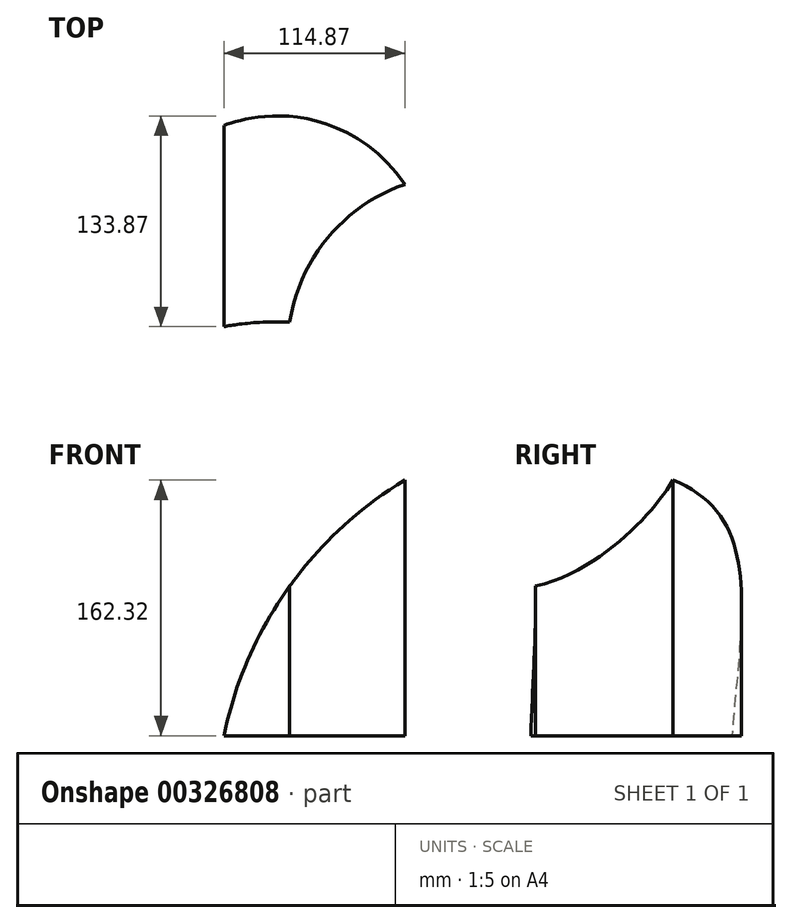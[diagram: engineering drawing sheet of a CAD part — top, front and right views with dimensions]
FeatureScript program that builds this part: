
annotation { "Feature Type Name" : "Feature", "Feature Type Description" : "" }
export const myFeature = defineFeature(function(context is Context, id is Id, definition is map)
    precondition{}
    {
        {
            var Q0;
            Q0=qCreatedBy(makeId("Top.planeOp"),FACE);
            var sketch = newSketch(context, id + "F0", { "sketchPlane" : qUnion([Q0])});
            skCircle(sketch, "E0", {"center": v(0, 280.6) * mm, "radius": 97.28 * mm});
            skCircle(sketch, "E1", {"center": v(117.11, 230) * mm, "radius": 110.4 * mm});
            skCircle(sketch, "E2", {"center": v(0, 58.68) * mm, "radius": 188.4 * mm});
            skSolve(sketch);
        }
        {
            var Q0;
            {var subQ0=sQuery(id+"F0.wireOp",EDGE,"E2");var subQ1=sQuery(id+"F0.wireOp",EDGE,"E0");var subQ2=makeQuery(id+"F0.imprint","INTERSECT",VERTEX,{"disambiguationData":[OD(0.0)],"derivedFrom":[subQ1,subQ0]});Q0=makeQuery(id+"F0.imprint","IMPRINT",FACE,{"disambiguationData":[TD([[makeQuery(id+"F0.imprint","IMPRINT",EDGE,{"disambiguationData":[TD([[subQ2,1.0]])],"derivedFrom":subQ1}),1.0]])]});}
            extrude(context, id + "F1", {"entities" : qUnion([Q0]), "depth" : 168.36 * mm});
        }
        {
            var Q0;
            Q0=qCreatedBy(makeId("Front.planeOp"),FACE);
            var sketch = newSketch(context, id + "F2", { "sketchPlane" : qUnion([Q0])});
            skCircle(sketch, "E3", {"center": v(209.61, -50.43) * mm, "radius": 248.57 * mm});
            skSolve(sketch);
        }
        {
            var Q0;
            Q0 = qSketchRegion(id + "F2", true);
            extrude(context, id + "F3", {"entities" : qUnion([Q0]), "oppositeDirection" : true, "depth" : 465.38 * mm});
        }
        {
            var Q0;
            Q0=makeQuery(id+"F1.opExtrude","SWEPT_BODY",BODY,{"disambiguationData":[OSD([sQuery(id+"F0.wireOp",EDGE,"E0"),sQuery(id+"F0.wireOp",EDGE,"E1"),sQuery(id+"F0.wireOp",EDGE,"E2")])]});
            var Q1;
            Q1=makeQuery(id+"F3.opExtrude","SWEPT_BODY",BODY,{"disambiguationData":[OSD([sQuery(id+"F2.wireOp",EDGE,"E3")])]});
            booleanBodies(context, id + "F4", {"operationType" : BooleanOperationType.INTERSECTION, "tools" : qUnion([Q0, Q1])});
        }
    });
